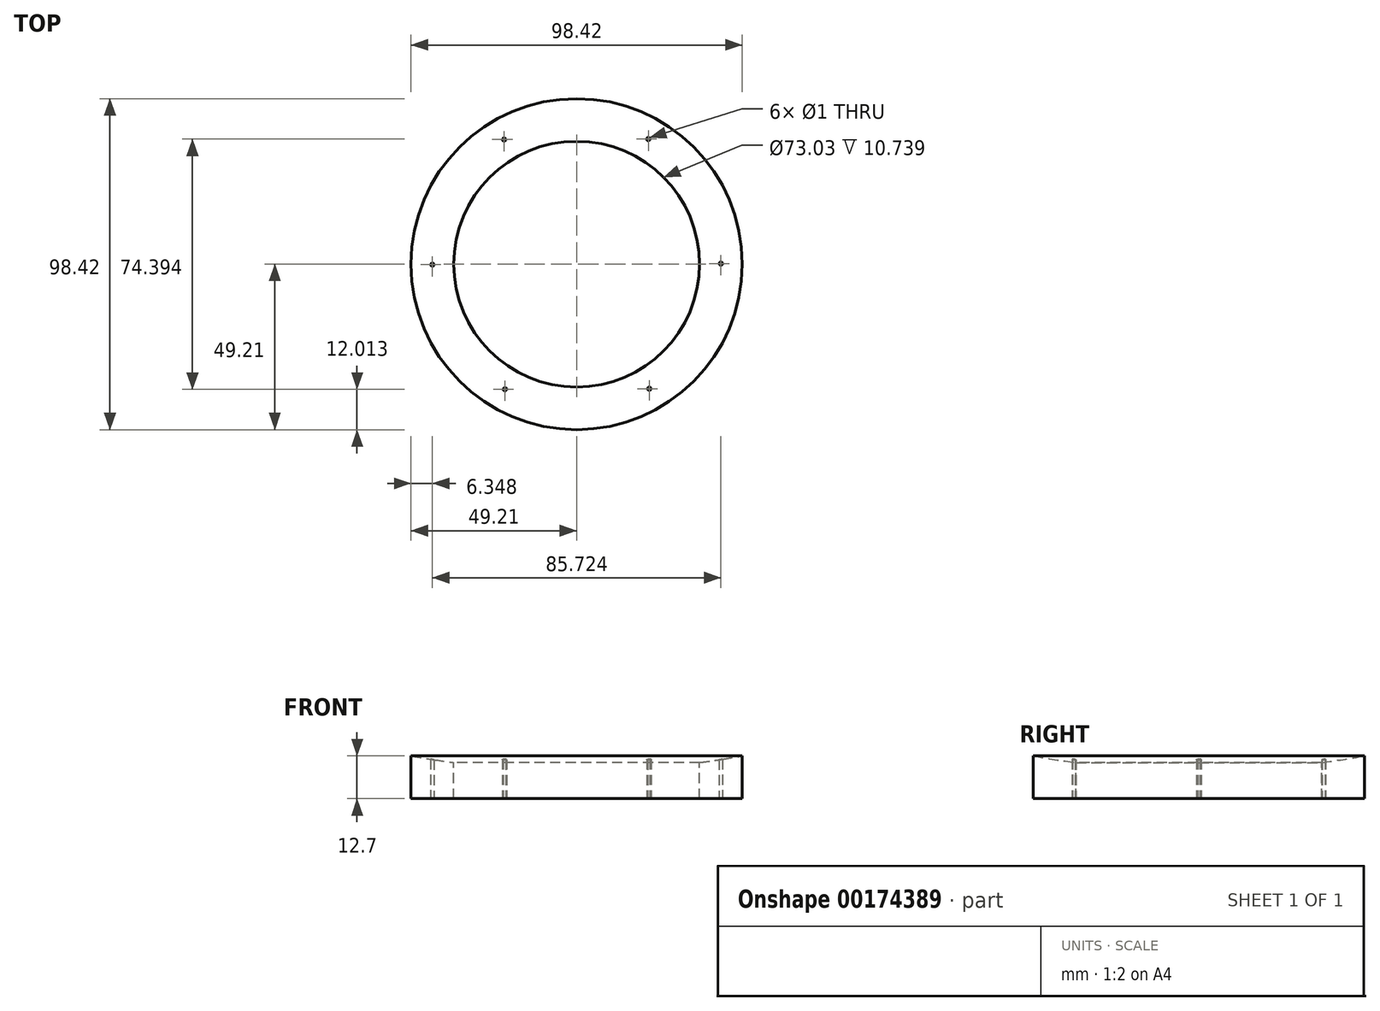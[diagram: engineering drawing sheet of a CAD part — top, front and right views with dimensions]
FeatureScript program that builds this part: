
annotation { "Feature Type Name" : "Feature", "Feature Type Description" : "" }
export const myFeature = defineFeature(function(context is Context, id is Id, definition is map)
    precondition{}
    {
        {
            var Q0;
            Q0=qCreatedBy(makeId("Top.planeOp"),FACE);
            var sketch = newSketch(context, id + "F0", { "sketchPlane" : qUnion([Q0])});
            skCircle(sketch, "E0", {"center": v(0, 0) * mm, "radius": 49.21 * mm});
            skSolve(sketch);
        }
        {
            var Q0;
            Q0=qCreatedBy(makeId("Front.planeOp"),FACE);
            var sketch = newSketch(context, id + "F1", { "sketchPlane" : qUnion([Q0])});
            skArc(sketch, "E1", {"start": v(-49.21, 12.7) * mm, "mid": v(0, 8.36) * mm, "end": v(49.21, 12.7) * mm});
            skPoint(sketch, "E2", {"position": v(0, 8.36) * mm});
            skLineSegment(sketch, "E3", {"start": v(49.21, 12.7) * mm, "end": v(49.21, 0) * mm});
            skLineSegment(sketch, "E4", {"start": v(0, 65.3) * mm, "end": v(0, -66.8) * mm, "construction": true});
            skLineSegment(sketch, "E5", {"start": v(36.51, 10.74) * mm, "end": v(36.51, 0) * mm});
            skLineSegment(sketch, "E6", {"start": v(36.51, 0) * mm, "end": v(49.21, 0) * mm});
            skSolve(sketch);
        }
        {
            var Q0;
            {var subQ0=sQuery(id+"F1.wireOp",EDGE,"E3");Q0=makeQuery(id+"F1.imprint","IMPRINT",FACE,{"disambiguationData":[TD([[makeQuery(id+"F1.imprint","IMPRINT",EDGE,{"derivedFrom":subQ0}),-1.0]])]});}
            var Q1;
            Q1=sQuery(id+"F1.wireOp",EDGE,"E4");
            revolve(context, id + "F2", {"entities" : qUnion([Q0]), "axis" : qUnion([Q1]), "revolveType" : RevolveType.FULL});
        }
        {
            var Q0;
            Q0=qCreatedBy(makeId("Top.planeOp"),FACE);
            var sketch = newSketch(context, id + "F3", { "sketchPlane" : qUnion([Q0])});
            skCircle(sketch, "E7.cCircle", {"center": v(0, 0) * mm, "radius": 42.86 * mm, "construction": true});
            skLineSegment(sketch, "E7.0", {"start": v(21.56, -37.04) * mm, "end": v(-21.3, -37.2) * mm});
            skLineSegment(sketch, "E7.1", {"start": v(-21.3, -37.2) * mm, "end": v(-42.86, -0.15) * mm});
            skLineSegment(sketch, "E7.2", {"start": v(-42.86, -0.15) * mm, "end": v(-21.56, 37.04) * mm});
            skLineSegment(sketch, "E7.3", {"start": v(-21.56, 37.04) * mm, "end": v(21.3, 37.2) * mm});
            skLineSegment(sketch, "E7.4", {"start": v(21.3, 37.2) * mm, "end": v(42.86, 0.15) * mm});
            skLineSegment(sketch, "E7.5", {"start": v(42.86, 0.15) * mm, "end": v(21.56, -37.04) * mm});
            skSolve(sketch);
        }
        {
            var Q0;
            Q0=sQuery(id+"F3.wireOp",VERTEX,"E7.1.start");
            var Q1;
            Q1=sQuery(id+"F3.wireOp",VERTEX,"E7.0.start");
            var Q2;
            Q2=sQuery(id+"F3.wireOp",VERTEX,"E7.5.start");
            var Q3;
            Q3=sQuery(id+"F3.wireOp",VERTEX,"E7.4.start");
            var Q4;
            Q4=sQuery(id+"F3.wireOp",VERTEX,"E7.3.start");
            var Q5;
            Q5=sQuery(id+"F3.wireOp",VERTEX,"E7.2.start");
            var Q6;
            Q6=makeQuery(id+"F2.opRevolve","SWEPT_BODY",BODY,{"disambiguationData":[OSD([sQuery(id+"F1.wireOp",EDGE,"E1"),sQuery(id+"F1.wireOp",EDGE,"E3"),sQuery(id+"F1.wireOp",EDGE,"E5"),sQuery(id+"F1.wireOp",EDGE,"E6")])]});
            hole(context, id + "F4", {"style" : HoleStyle.SIMPLE, "endStyle" : HoleEndStyle.THROUGH, "oppositeDirection" : true, "standardTappedOrClearance" : lookupTablePath({ "standard" : "ISO", "size" : "1", "type" : "Drilled" }), "standardBlindInLast" : lookupTablePath({ "standard" : "ISO", "size" : "1", "type" : "Drilled" }), "holeDiameter" : 1 * mm, "locations" : qUnion([Q0, Q1, Q2, Q3, Q4, Q5]), "scope" : qUnion([Q6]), "isTappedThrough" : true});
        }
    });
